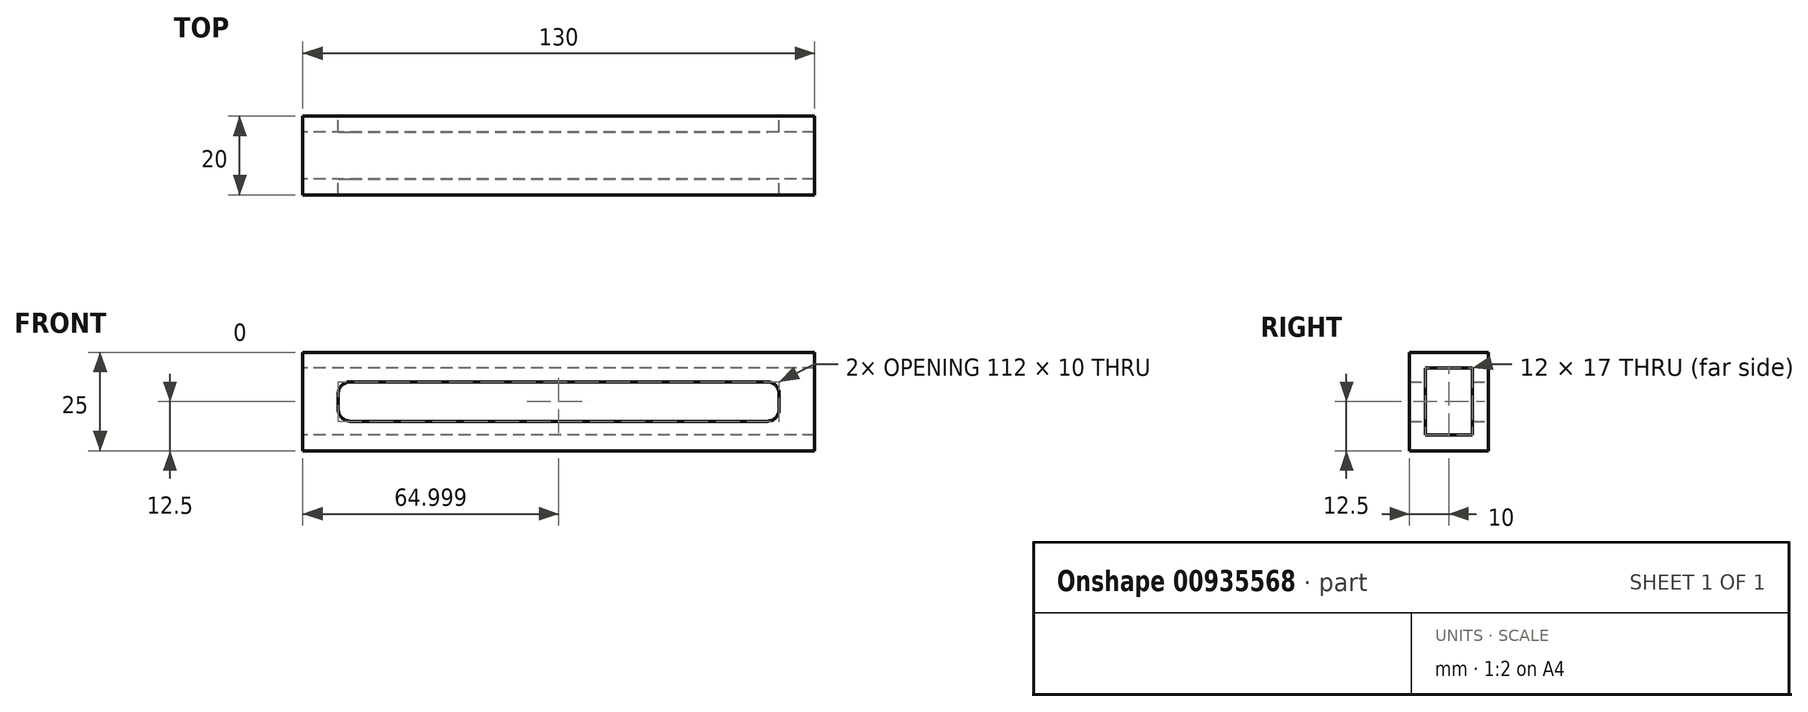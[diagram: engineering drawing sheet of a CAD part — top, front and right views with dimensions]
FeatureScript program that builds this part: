
annotation { "Feature Type Name" : "Feature", "Feature Type Description" : "" }
export const myFeature = defineFeature(function(context is Context, id is Id, definition is map)
    precondition{}
    {
        {
            var Q0;
            Q0=qCreatedBy(makeId("Front.planeOp"),FACE);
            var sketch = newSketch(context, id + "F0", { "sketchPlane" : qUnion([Q0])});
            skLineSegment(sketch, "E0.bottom", {"start": v(-65.51, 0) * mm, "end": v(64.49, 0) * mm});
            skLineSegment(sketch, "E0.top", {"start": v(-65.51, -25) * mm, "end": v(64.49, -25) * mm});
            skLineSegment(sketch, "E0.left", {"start": v(-65.51, 0) * mm, "end": v(-65.51, -25) * mm});
            skLineSegment(sketch, "E0.right", {"start": v(64.49, 0) * mm, "end": v(64.49, -25) * mm});
            skLineSegment(sketch, "E1.bottom", {"start": v(-53.51, -7.5) * mm, "end": v(52.49, -7.5) * mm});
            skLineSegment(sketch, "E1.top", {"start": v(-53.51, -17.5) * mm, "end": v(52.49, -17.5) * mm});
            skLineSegment(sketch, "E1.left", {"start": v(-56.51, -10.5) * mm, "end": v(-56.51, -14.5) * mm});
            skLineSegment(sketch, "E1.right", {"start": v(55.49, -10.5) * mm, "end": v(55.49, -14.5) * mm});
            skPoint(sketch, "E2.visualSharp", {"position": v(-56.51, -7.5) * mm});
            skArc(sketch, "E2.filletArc", {"start": v(-53.51, -7.5) * mm, "mid": v(-55.63, -8.38) * mm, "end": v(-56.51, -10.5) * mm});
            skPoint(sketch, "E3.visualSharp", {"position": v(-56.51, -17.5) * mm});
            skArc(sketch, "E3.filletArc", {"start": v(-56.51, -14.5) * mm, "mid": v(-55.63, -16.62) * mm, "end": v(-53.51, -17.5) * mm});
            skPoint(sketch, "E4.visualSharp", {"position": v(55.49, -17.5) * mm});
            skArc(sketch, "E4.filletArc", {"start": v(52.49, -17.5) * mm, "mid": v(54.6, -16.62) * mm, "end": v(55.49, -14.5) * mm});
            skPoint(sketch, "E5.visualSharp", {"position": v(55.49, -7.5) * mm});
            skArc(sketch, "E5.filletArc", {"start": v(55.49, -10.5) * mm, "mid": v(54.6, -8.38) * mm, "end": v(52.49, -7.5) * mm});
            skSolve(sketch);
        }
        {
            var Q0;
            Q0=makeQuery(id+"F0.imprint","IMPRINT",FACE,{"disambiguationData":[TD([[makeQuery(id+"F0.imprint","IMPRINT",EDGE,{"derivedFrom":sQuery(id+"F0.wireOp",EDGE,"E0.bottom")}),-1.0]])]});
            extrude(context, id + "F1", {"entities" : qUnion([Q0]), "endBound" : BoundingType.SYMMETRIC, "depth" : 20 * mm, "offsetDistance" : 25 * mm});
        }
        {
            var Q0;
            Q0=qCreatedBy(makeId("Right.planeOp"),FACE);
            var sketch = newSketch(context, id + "F2", { "sketchPlane" : qUnion([Q0])});
            skLineSegment(sketch, "E6", {"start": v(0, 0) * mm, "end": v(0, -25) * mm, "construction": true});
            skLineSegment(sketch, "E7", {"start": v(10.02, -12.5) * mm, "end": v(-9.97, -12.5) * mm, "construction": true});
            skLineSegment(sketch, "E8.bottom", {"start": v(6, -21) * mm, "end": v(-6, -21) * mm});
            skLineSegment(sketch, "E8.top", {"start": v(6, -4) * mm, "end": v(-6, -4) * mm});
            skLineSegment(sketch, "E8.left", {"start": v(6, -21) * mm, "end": v(6, -4) * mm});
            skLineSegment(sketch, "E8.right", {"start": v(-6, -21) * mm, "end": v(-6, -4) * mm});
            skPoint(sketch, "E8.middle", {"position": v(0, -12.5) * mm});
            skSolve(sketch);
        }
        {
            var Q0;
            Q0=makeQuery(id+"F2.imprint","IMPRINT",FACE,{"disambiguationData":[TD([[makeQuery(id+"F2.imprint","IMPRINT",EDGE,{"derivedFrom":sQuery(id+"F2.wireOp",EDGE,"E8.bottom")}),-1.0]])]});
            extrude(context, id + "F3", {"entities" : qUnion([Q0]), "operationType" : NewBodyOperationType.REMOVE, "endBound" : BoundingType.SYMMETRIC, "depth" : 172.6 * mm, "offsetDistance" : 25 * mm});
        }
    });
